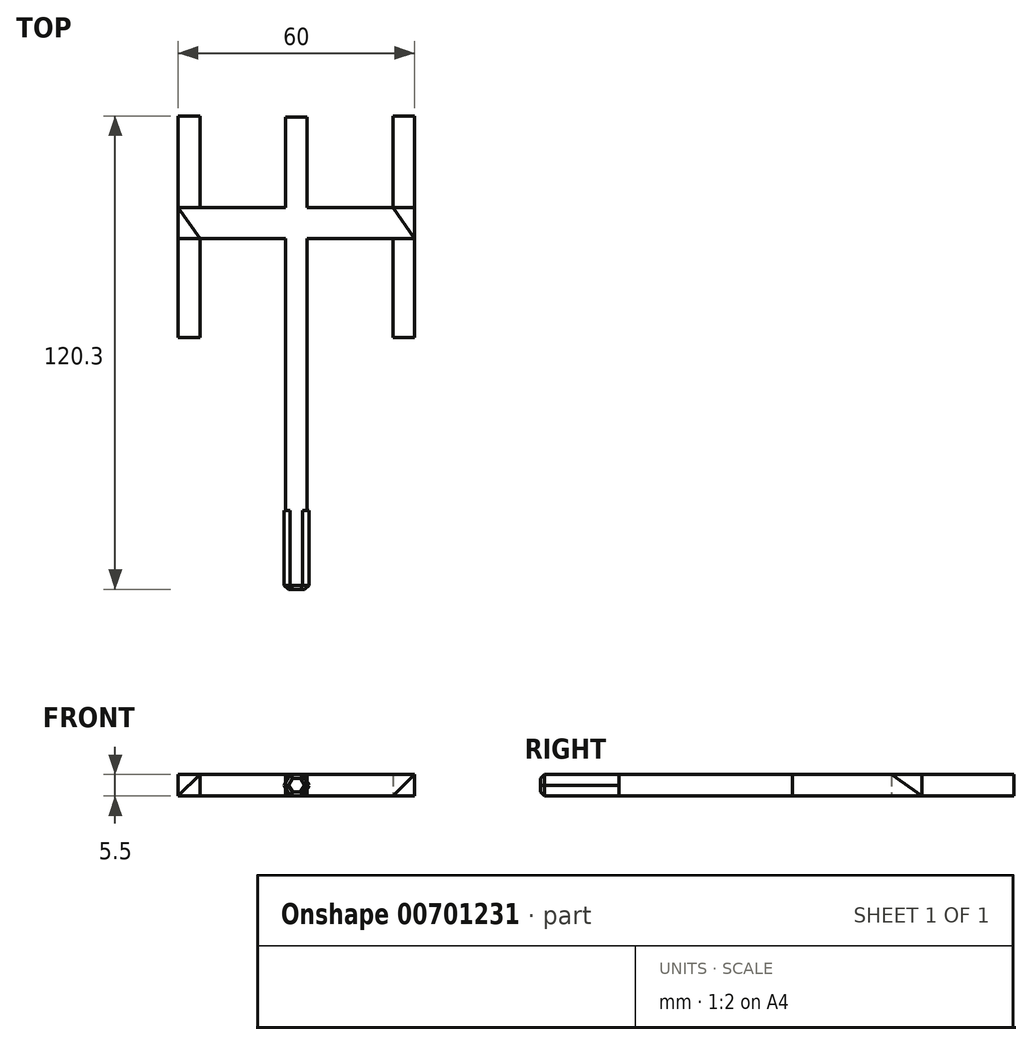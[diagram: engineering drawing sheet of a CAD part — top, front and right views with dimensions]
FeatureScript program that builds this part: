
annotation { "Feature Type Name" : "Feature", "Feature Type Description" : "" }
export const myFeature = defineFeature(function(context is Context, id is Id, definition is map)
    precondition{}
    {
        {
            assignVariable(context, id + "F0", {"name" : "Thickness", "anyValue" : 5.5});
        }
        {
            var Q0;
            Q0=qCreatedBy(makeId("Top.planeOp"),FACE);
            var sketch = newSketch(context, id + "F1", { "sketchPlane" : qUnion([Q0])});
            skLineSegment(sketch, "E0.bottom", {"start": v(-65.45, 75.29) * mm, "end": v(-59.95, 75.29) * mm});
            skLineSegment(sketch, "E0.top", {"start": v(-65.45, -24.71) * mm, "end": v(-59.95, -24.71) * mm});
            skLineSegment(sketch, "E0.left", {"start": v(-65.45, 75.29) * mm, "end": v(-65.45, 52.28) * mm});
            skLineSegment(sketch, "E0.right", {"start": v(-59.95, 75.29) * mm, "end": v(-59.95, 52.28) * mm});
            skLineSegment(sketch, "E1", {"start": v(-59.95, 44.47) * mm, "end": v(-38.2, 44.47) * mm});
            skLineSegment(sketch, "E2", {"start": v(-38.2, 44.47) * mm, "end": v(-38.2, 19.27) * mm});
            skLineSegment(sketch, "E3", {"start": v(-38.2, 19.27) * mm, "end": v(-32.7, 19.27) * mm});
            skLineSegment(sketch, "E4", {"start": v(-32.7, 19.27) * mm, "end": v(-32.7, 75.59) * mm});
            skLineSegment(sketch, "E5", {"start": v(-32.7, 75.59) * mm, "end": v(-38.2, 75.59) * mm});
            skLineSegment(sketch, "E6", {"start": v(-62.7, 75.29) * mm, "end": v(-62.7, -24.71) * mm, "construction": true});
            skLineSegment(sketch, "E7.MirrorCS", {"start": v(-65.45, 44.47) * mm, "end": v(-87.2, 44.47) * mm});
            skLineSegment(sketch, "E8.MirrorCS", {"start": v(-87.2, 44.47) * mm, "end": v(-87.2, 19.27) * mm});
            skLineSegment(sketch, "E9.MirrorCS", {"start": v(-87.2, 19.27) * mm, "end": v(-92.7, 19.27) * mm});
            skLineSegment(sketch, "E10.MirrorCS", {"start": v(-92.7, 19.27) * mm, "end": v(-92.7, 75.59) * mm});
            skLineSegment(sketch, "E11.MirrorCS", {"start": v(-92.7, 75.59) * mm, "end": v(-87.2, 75.59) * mm});
            skLineSegment(sketch, "E12.trimOffspring", {"start": v(-59.95, 44.47) * mm, "end": v(-59.95, -24.71) * mm});
            skLineSegment(sketch, "E13.trimOffspring", {"start": v(-65.45, 44.47) * mm, "end": v(-65.45, -24.71) * mm});
            skLineSegment(sketch, "E14", {"start": v(-38.2, 52.28) * mm, "end": v(-38.2, 75.59) * mm});
            skLineSegment(sketch, "E15", {"start": v(-38.2, 52.28) * mm, "end": v(-59.95, 52.28) * mm});
            skLineSegment(sketch, "E16.MirrorCS", {"start": v(-87.2, 52.28) * mm, "end": v(-87.2, 75.59) * mm});
            skLineSegment(sketch, "E17.MirrorCS", {"start": v(-87.2, 52.28) * mm, "end": v(-65.45, 52.28) * mm});
            skSolve(sketch);
        }
        {
            var Q0;
            Q0=makeQuery(id+"F1.imprint","IMPRINT",FACE,{"disambiguationData":[TD([[makeQuery(id+"F1.imprint","IMPRINT",EDGE,{"derivedFrom":sQuery(id+"F1.wireOp",EDGE,"E0.bottom")}),-1.0]])]});
            extrude(context, id + "F2", {"entities" : qUnion([Q0]), "depth" : (getVariable(context, 'Thickness')) * mm, "offsetDistance" : 25 * mm});
        }
        {
            var Q0;
            Q0=makeQuery(id+"F2.opExtrude","SWEPT_FACE",FACE,{"disambiguationData":[OSD([sQuery(id+"F1.wireOp",EDGE,"E0.top")])]});
            var sketch = newSketch(context, id + "F3", { "sketchPlane" : qUnion([Q0])});
            skCircle(sketch, "E18.cCircle", {"center": v(-62.7, 2.75) * mm, "radius": 3.18 * mm, "construction": true});
            skLineSegment(sketch, "E18.0", {"start": v(-61.1, 0) * mm, "end": v(-64.28, 0) * mm});
            skLineSegment(sketch, "E18.1", {"start": v(-64.28, 0) * mm, "end": v(-65.87, 2.75) * mm});
            skLineSegment(sketch, "E18.2", {"start": v(-65.87, 2.75) * mm, "end": v(-64.28, 5.5) * mm});
            skLineSegment(sketch, "E18.3", {"start": v(-64.28, 5.5) * mm, "end": v(-61.1, 5.5) * mm});
            skLineSegment(sketch, "E18.4", {"start": v(-61.1, 5.5) * mm, "end": v(-59.52, 2.75) * mm});
            skLineSegment(sketch, "E18.5", {"start": v(-59.52, 2.75) * mm, "end": v(-61.1, 0) * mm});
            skLineSegment(sketch, "E19", {"start": v(-65.45, 5.5) * mm, "end": v(-59.95, 0) * mm, "construction": true});
            skLineSegment(sketch, "E20", {"start": v(-59.95, 5.5) * mm, "end": v(-65.45, 0) * mm, "construction": true});
            skSolve(sketch);
        }
        {
            var Q0;
            Q0 = qSketchRegion(id + "F3", true);
            extrude(context, id + "F4", {"entities" : qUnion([Q0]), "operationType" : NewBodyOperationType.ADD, "depth" : 20 * mm, "offsetDistance" : 25 * mm});
        }
        {
            var Q0;
            Q0=makeQuery(id+"F4.opExtrude","CAP_FACE",FACE,{"disambiguationData":[OSD([sQuery(id+"F3.wireOp",EDGE,"E18.0"),sQuery(id+"F3.wireOp",EDGE,"E18.1"),sQuery(id+"F3.wireOp",EDGE,"E18.2"),sQuery(id+"F3.wireOp",EDGE,"E18.3"),sQuery(id+"F3.wireOp",EDGE,"E18.4"),sQuery(id+"F3.wireOp",EDGE,"E18.5")])],"isStart":false});
            chamfer(context, id + "F5", {"entities" : qUnion([Q0]), "width" : 1 * mm, "tangentPropagation" : true});
        }
        {
            var Q0;
            Q0=makeQuery(id+"F2.opExtrude","SWEPT_FACE",FACE,{"disambiguationData":[OSD([sQuery(id+"F1.wireOp",EDGE,"E3")])]});
            var sketch = newSketch(context, id + "F6", { "sketchPlane" : qUnion([Q0])});
            skLineSegment(sketch, "E21", {"start": v(-38.2, 0) * mm, "end": v(-32.7, 5.5) * mm});
            skLineSegment(sketch, "E22", {"start": v(-32.7, 5.5) * mm, "end": v(-38.2, 5.5) * mm});
            skLineSegment(sketch, "E23", {"start": v(-38.2, 5.5) * mm, "end": v(-38.2, 0) * mm});
            skLineSegment(sketch, "E24", {"start": v(-92.7, 0) * mm, "end": v(-87.2, 5.5) * mm});
            skLineSegment(sketch, "E25", {"start": v(-92.7, 0) * mm, "end": v(-92.7, 5.5) * mm});
            skLineSegment(sketch, "E26", {"start": v(-92.7, 5.5) * mm, "end": v(-87.2, 5.5) * mm});
            skSolve(sketch);
        }
        {
            var Q0;
            Q0 = qSketchRegion(id + "F6", true);
            var Q1;
            Q1=makeQuery(id+"F2.opExtrude","SWEPT_FACE",FACE,{"disambiguationData":[OSD([sQuery(id+"F1.wireOp",EDGE,"E1")])]});
            extrude(context, id + "F7", {"entities" : qUnion([Q0]), "operationType" : NewBodyOperationType.REMOVE, "endBound" : BoundingType.UP_TO_SURFACE, "oppositeDirection" : true, "depth" : 25 * mm, "endBoundEntityFace" : qUnion([Q1]), "offsetDistance" : 25 * mm});
        }
        {
            var Q0;
            Q0=makeQuery(id+"F2.opExtrude","SWEPT_FACE",FACE,{"disambiguationData":[OSD([sQuery(id+"F1.wireOp",EDGE,"E5")])]});
            var sketch = newSketch(context, id + "F8", { "sketchPlane" : qUnion([Q0])});
            skLineSegment(sketch, "E27", {"start": v(38.2, 5.5) * mm, "end": v(32.7, 0) * mm});
            skLineSegment(sketch, "E28", {"start": v(92.7, 5.5) * mm, "end": v(87.2, 0) * mm});
            skLineSegment(sketch, "E29", {"start": v(87.2, 0) * mm, "end": v(87.2, 5.5) * mm});
            skLineSegment(sketch, "E30", {"start": v(87.2, 5.5) * mm, "end": v(92.7, 5.5) * mm});
            skLineSegment(sketch, "E31", {"start": v(32.7, 0) * mm, "end": v(32.7, 5.5) * mm});
            skLineSegment(sketch, "E32", {"start": v(32.7, 5.5) * mm, "end": v(38.2, 5.5) * mm});
            skSolve(sketch);
        }
        {
            var Q0;
            Q0 = qSketchRegion(id + "F8", true);
            var Q1;
            Q1=makeQuery(id+"F2.opExtrude","SWEPT_FACE",FACE,{"disambiguationData":[OSD([sQuery(id+"F1.wireOp",EDGE,"E15")])]});
            extrude(context, id + "F9", {"entities" : qUnion([Q0]), "operationType" : NewBodyOperationType.REMOVE, "endBound" : BoundingType.UP_TO_SURFACE, "oppositeDirection" : true, "depth" : 25 * mm, "endBoundEntityFace" : qUnion([Q1]), "offsetDistance" : 25 * mm});
        }
        {
            var Q0;
            {var subQ0=sQuery(id+"F1.wireOp",EDGE,"E15");var subQ1=sQuery(id+"F1.wireOp",EDGE,"E14");Q0=makeQuery(id+"F9.boolean.opBoolean","MERGE",VERTEX,{"derivedFrom":[makeQuery(id+"F2.opExtrude","CAP_VERTEX",VERTEX,{"disambiguationData":[OSD([subQ1,subQ0])],"isStart":false}),makeQuery(id+"F9.opExtrude","CAP_VERTEX",VERTEX,{"disambiguationData":[OSD([sQuery(id+"F1.wireOp",EDGE,"E5"),subQ1,subQ0,sQuery(id+"F8.wireOp",EDGE,"E27"),sQuery(id+"F8.wireOp",EDGE,"E32")])],"isStart":false})]});}
            var Q1;
            Q1=makeQuery(id+"F9.boolean.opBoolean","COPY",VERTEX,{"derivedFrom":makeQuery(id+"F9.opExtrude","CAP_VERTEX",VERTEX,{"disambiguationData":[OSD([sQuery(id+"F1.wireOp",EDGE,"E5"),sQuery(id+"F1.wireOp",EDGE,"E15"),sQuery(id+"F8.wireOp",EDGE,"E27"),sQuery(id+"F8.wireOp",EDGE,"E31")])],"isStart":false})});
            var Q2;
            Q2=makeQuery(id+"F7.boolean.opBoolean","COPY",VERTEX,{"derivedFrom":makeQuery(id+"F7.opExtrude","CAP_VERTEX",VERTEX,{"disambiguationData":[OSD([sQuery(id+"F1.wireOp",EDGE,"E1"),sQuery(id+"F1.wireOp",EDGE,"E3"),sQuery(id+"F1.wireOp",EDGE,"E4"),sQuery(id+"F6.wireOp",EDGE,"E21"),sQuery(id+"F6.wireOp",EDGE,"E22")])],"isStart":false})});
            cPlane(context, id + "F10", {"entities" : qUnion([Q0, Q1, Q2]), "cplaneType" : CPlaneType.THREE_POINT, "offset" : 25 * mm, "width" : 150 * mm, "height" : 150 * mm});
        }
        {
            var Q0;
            Q0=qCreatedBy(id+"F10.planeOp",FACE);
            var sketch = newSketch(context, id + "F11", { "sketchPlane" : qUnion([Q0])});
            skLineSegment(sketch, "E33", {"start": v(48.38, 27) * mm, "end": v(57.1, 23.12) * mm});
            skLineSegment(sketch, "E34", {"start": v(57.1, 23.12) * mm, "end": v(57.1, 30.9) * mm});
            skLineSegment(sketch, "E35", {"start": v(57.1, 30.9) * mm, "end": v(48.38, 27) * mm});
            skSolve(sketch);
        }
        {
            var Q0;
            Q0 = qSketchRegion(id + "F11", true);
            var Q1;
            Q1=makeQuery(id+"F9.boolean.opBoolean","COPY",VERTEX,{"derivedFrom":makeQuery(id+"F9.opExtrude","CAP_VERTEX",VERTEX,{"disambiguationData":[OSD([sQuery(id+"F1.wireOp",EDGE,"E15"),sQuery(id+"F8.wireOp",EDGE,"E31"),sQuery(id+"F8.wireOp",EDGE,"E32")])],"isStart":false})});
            extrude(context, id + "F12", {"entities" : qUnion([Q0]), "operationType" : NewBodyOperationType.REMOVE, "endBound" : BoundingType.UP_TO_VERTEX, "depth" : 25 * mm, "endBoundEntityVertex" : qUnion([Q1]), "offsetDistance" : 25 * mm});
        }
        {
            var Q0;
            Q0=makeQuery(id+"F7.boolean.opBoolean","COPY",VERTEX,{"derivedFrom":makeQuery(id+"F7.opExtrude","CAP_VERTEX",VERTEX,{"disambiguationData":[OSD([sQuery(id+"F1.wireOp",EDGE,"E1"),sQuery(id+"F6.wireOp",EDGE,"E24"),sQuery(id+"F6.wireOp",EDGE,"E25")])],"isStart":false})});
            var Q1;
            Q1=makeQuery(id+"F7.boolean.opBoolean","MERGE",VERTEX,{"derivedFrom":[makeQuery(id+"F2.opExtrude","CAP_VERTEX",VERTEX,{"disambiguationData":[OSD([sQuery(id+"F1.wireOp",EDGE,"E7.MirrorCS"),sQuery(id+"F1.wireOp",EDGE,"E8.MirrorCS")])],"isStart":false}),makeQuery(id+"F7.opExtrude","CAP_VERTEX",VERTEX,{"disambiguationData":[OSD([sQuery(id+"F1.wireOp",EDGE,"E1"),sQuery(id+"F6.wireOp",EDGE,"E24"),sQuery(id+"F6.wireOp",EDGE,"E26")])],"isStart":false})]});
            var Q2;
            Q2=makeQuery(id+"F9.boolean.opBoolean","COPY",VERTEX,{"derivedFrom":makeQuery(id+"F9.opExtrude","CAP_VERTEX",VERTEX,{"disambiguationData":[OSD([sQuery(id+"F1.wireOp",EDGE,"E15"),sQuery(id+"F8.wireOp",EDGE,"E28"),sQuery(id+"F8.wireOp",EDGE,"E30")])],"isStart":false})});
            cPlane(context, id + "F13", {"entities" : qUnion([Q0, Q1, Q2]), "cplaneType" : CPlaneType.THREE_POINT, "offset" : 25 * mm, "width" : 150 * mm, "height" : 150 * mm});
        }
        {
            var Q0;
            Q0=qCreatedBy(id+"F13.planeOp",FACE);
            var sketch = newSketch(context, id + "F14", { "sketchPlane" : qUnion([Q0])});
            skLineSegment(sketch, "E36", {"start": v(77.75, -61.66) * mm, "end": v(69.03, -65.55) * mm});
            skLineSegment(sketch, "E37", {"start": v(69.03, -65.55) * mm, "end": v(69.03, -57.77) * mm});
            skLineSegment(sketch, "E38", {"start": v(69.03, -57.77) * mm, "end": v(77.75, -61.66) * mm});
            skSolve(sketch);
        }
        {
            var Q0;
            Q0 = qSketchRegion(id + "F14", true);
            var Q1;
            Q1=makeQuery(id+"F7.boolean.opBoolean","COPY",VERTEX,{"derivedFrom":makeQuery(id+"F7.opExtrude","CAP_VERTEX",VERTEX,{"disambiguationData":[OSD([sQuery(id+"F1.wireOp",EDGE,"E1"),sQuery(id+"F6.wireOp",EDGE,"E25"),sQuery(id+"F6.wireOp",EDGE,"E26")])],"isStart":false})});
            extrude(context, id + "F15", {"entities" : qUnion([Q0]), "operationType" : NewBodyOperationType.REMOVE, "endBound" : BoundingType.UP_TO_VERTEX, "oppositeDirection" : true, "depth" : 25 * mm, "endBoundEntityVertex" : qUnion([Q1]), "offsetDistance" : 25 * mm});
        }
    });
